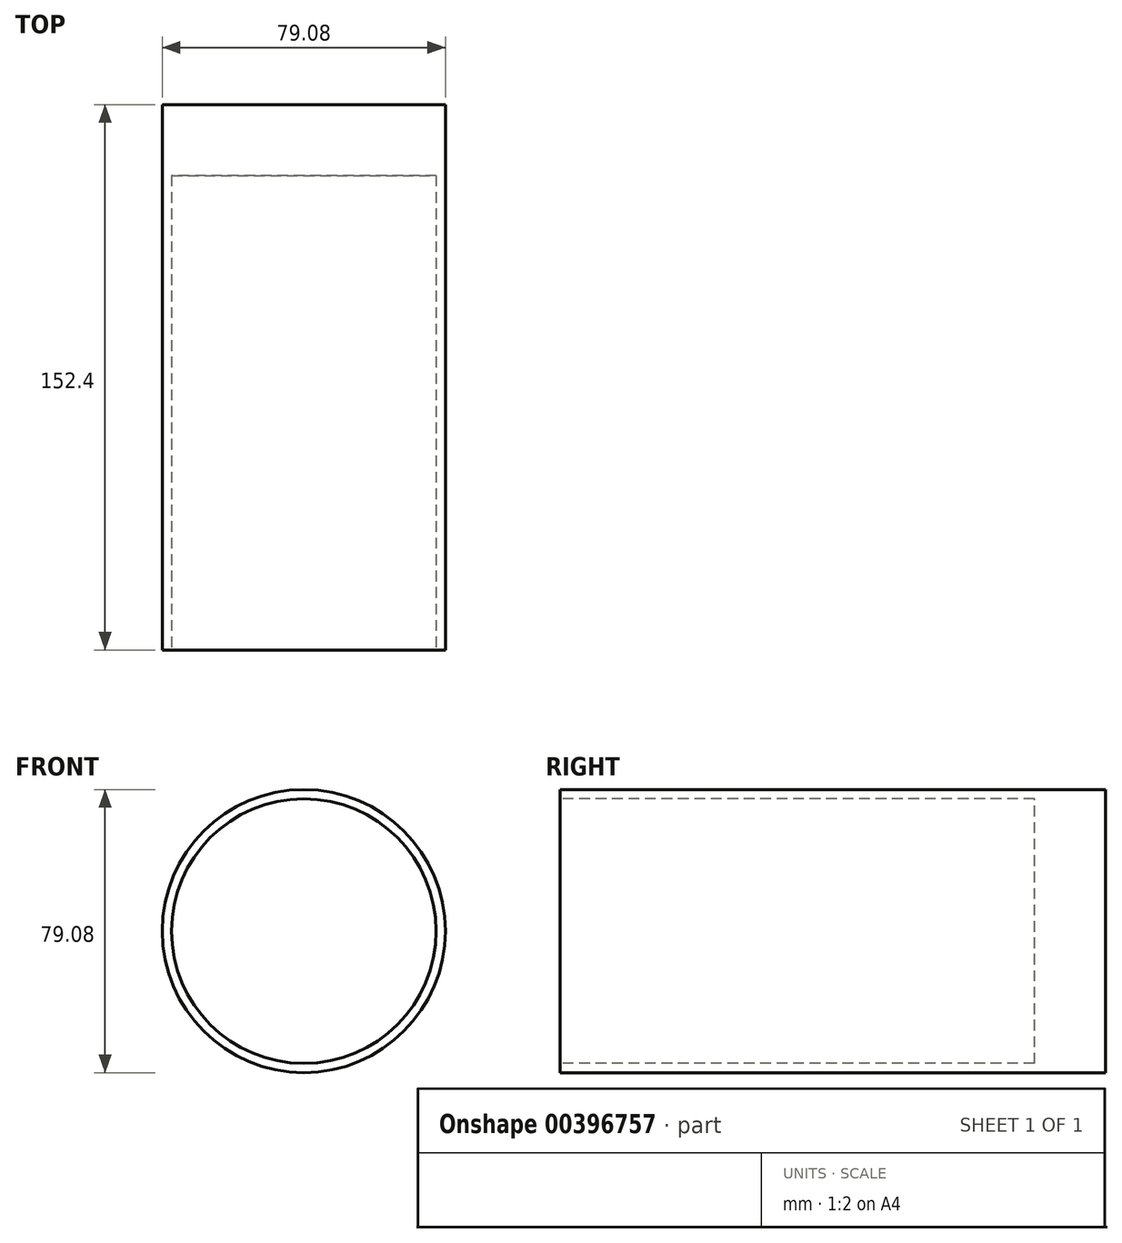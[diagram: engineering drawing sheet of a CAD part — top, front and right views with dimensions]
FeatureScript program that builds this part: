
annotation { "Feature Type Name" : "Feature", "Feature Type Description" : "" }
export const myFeature = defineFeature(function(context is Context, id is Id, definition is map)
    precondition{}
    {
        {
            var Q0;
            Q0=qCreatedBy(makeId("Front.planeOp"),FACE);
            var sketch = newSketch(context, id + "F0", { "sketchPlane" : qUnion([Q0])});
            skCircle(sketch, "E0", {"center": v(0, 0) * mm, "radius": 39.54 * mm});
            skSolve(sketch);
        }
        {
            var Q0;
            Q0 = qSketchRegion(id + "F0", true);
            var Q1;
            Q1 = qSketchRegion(id + "F2", true);
            extrude(context, id + "F1", {"entities" : qUnion([Q0, Q1]), "depth" : 152.4 * mm});
        }
        {
            var Q0;
            Q0=makeQuery(id+"F1.opExtrude","CAP_FACE",FACE,{"disambiguationData":[OSD([sQuery(id+"F0.wireOp",EDGE,"E0")])],"isStart":false});
            var sketch = newSketch(context, id + "F2", { "sketchPlane" : qUnion([Q0])});
            skCircle(sketch, "E1", {"center": v(0, 0) * mm, "radius": 36.97 * mm});
            skSolve(sketch);
        }
        {
            var Q0;
            Q0 = qSketchRegion(id + "F2", true);
            extrude(context, id + "F3", {"entities" : qUnion([Q0]), "operationType" : NewBodyOperationType.REMOVE, "oppositeDirection" : true, "depth" : 132.6 * mm});
        }
    });
